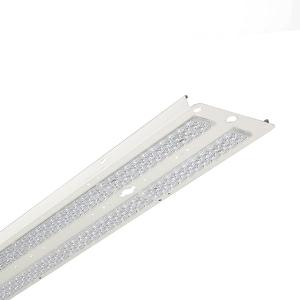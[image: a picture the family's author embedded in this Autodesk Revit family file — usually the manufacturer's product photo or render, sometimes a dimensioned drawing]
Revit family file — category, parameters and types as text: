
# Revit family: 3f_filippi_-_kit_led_retrofit_per_schermo_in_vetro_3f_filippi_-_a5212_-_kit_led_i3f_76_a3f_91_-_l1565_-__7bcecbea5744f0cb
name_source: partatom
category: Lighting Fixtures
units: mm (PartAtom-declared; Revit-internal decimal feet)

## family parameters
Cut with Voids When Loaded = No
Host = Face
Light Source = No
Part Type = Normal
Room Calculation Point = No
Round Connector Dimension = Use Diameter
Shared = No

## types (1)
- 3F Filippi - Kit LED Retrofit per schermo in vetro (1 x LED, 11260 lm, 74 W, 4000 K)
    Apparent Load = 74 VA
    Approval mark = ENEC
    CIE Flux Codes = 77 93 99 100 100
    Color Rendering = 80
    Color Temperature = 4000 K
    Control Gear = Electronic ballast
    Default Elevation = 1800 mm
    Description = Led retrofit kit suitable for Fluorescent Beta 2x i3F 76 and A3F 91 luminaires.

ILLUMINOTECHNICAL
Luminous efficiency 100% (DLOR 100%, ULOR 0%).
Initial luminous flux of the luminaire 11260 lm.
Symmetric concentrated distribution.
Installation Interdistance Transv.D = 0.57 x hu - Long.D = 1.12 x hu.
Tabular UGR (CIE 117 - 4H-8H; S=0.25H; 70/50/20): RUG 17.5 - 19.7.
Beam angle: 36° - 73°.
Luminous efficacy 152 lm/W.
Lifetime (L93/B10): 30000 h. (tq+25°C)
Lifetime (L90/B10): 50000 h. (tq+25°C)
Lifetime (L85/B10): 80000 h. (tq+25°C)
Lifetime (L80/B10): 100000 h. (tq+25°C)
Lifetime (L85/B10): 50000 h. (tq+40°C)
Sudden decreased luminous flux after 50000 hours: 0% (C0).
Photobiological safety in compliance with IEC/TR 62778: RG0 risk exempt, (IEC 62471).
In compliance with IEC/EN 62722-2-1 - IEC/EN 62717 standards.

SOURCE
2 linear LED modules 40W/840.
Energy efficiency class (UE 2019/2020 - UE 2019/2015): C.
CIE 13.3 Colour rendering index: CRI >80 (R9 <50%).
IES TM-30 Fidelity Index: Rf = 84 Rg = 95.
CCT nominal colour temperature 4000 K.
Colour initial tolerance (MacAdam): SDCM 3.

MECHANICAL
Gear-tray unit in hot-galvanised steel, painted in white polyester, fixed to the housing by means of "Ribloc" rapid devices in galvanised steel, hinged opening.
Transparent methacrylate (PMMA) concentrated distribution lenses with flat external surface.
Luminaire with limited surface temperature. - D - (EN 60598-2-24)
Dimensions: 1565x235 mm, height 105 mm. Weight 3.395 kg.
Glow-wire test resistance 850°C.

ELECTRICAL
Halogen Free electronic wiring 230V-50/60Hz, power factor 0.95, THD <25%, constant output current, class I, 1 driver.
Power of the luminaire 74 W.
CE - IEC 60598-1 - EN 60598-1.
SAFE FLICKER: PstLM=<1 and SVM=<0.4 (IEC TR 61547-1 and IEC TR 63158), to ensure a more comfortable and safe light.
Luminaire compliant with EN 60598-2-22 for power supply from a centralised emergency system CPSS (Central Power Supply System), not incorporated in the luminaire - high risk areas excluded. The default power and flux are 100% in AC and 100% in DC.
Ambient temperature from -20°C to +40°C.
Temperature class T6 max 85°C.
Relative humidity UR: <85%.

INSTALLATION
Retrofit.
Correct installation of the retrofit LED kit, compliant with EN 60598-1 and CE marked, inside the 3F Filippi - Beta 2x i3F 76 and A3F 91 Fluorescent luminaires must be only carried out by qualified personnel to ensure compliance with the national installation standards.
Attention: to maintain the degree of protection of the device and for the purposes of validity of the guarantee of the new retrofit kits, it is imperative to replace the old cable guides (on the body of the device) with the new ones supplied.
All accessories dedicated to this product are available on the Catalog and on our website www.3F-Filippi.com.

WARNING
Fixture not suitable for cold stores with an ambient temperature <0°C and/or relative humidity >85%.
Luminaire designed for disposal/recycling at end-of-life.
Replaceable (LED only) light source by a professional. Replaceable control gear by a professional.
    Height = 105 mm
    Lamp = 1 x LED
    Lamp Light Flux = 11260 lm
    Lamp Power = 74 W
    Lamp count = 1
    Length = 1565 mm
    Lifetime = 50000 h
    Luminous efficacy = 152 lm/W
    Manufacturer = 3F Filippi
    ModVariant = No
    Model = 3F Filippi - A5212 - Kit LED i3F 76,A3F 91 - L1565 - L 2x40W CONC
    Mounting Place = Ceiling
    Mounting Type = Surface mounted
    Number of Poles = 1
    OnlyDefault = Yes
    Power Factor = 1
    Product Name = 3F Filippi - Kit LED Retrofit per schermo in vetro
    Product group = ceiling mounted luminaire
    ProductGroupID = 3
    Protection Class = Protection class I
    Protection Degree = Degree of protection
    RLX_Detail_Level = 1
    RLX_Emergency_Light_Flux = 0 lm
    RLX_Emergency_Type = 0
    RLX_Emergency_Type_DB = No
    RlxData = <blob elided: 68885 chars, md5=a219a7c4>
    Socket = socket
    Standby Power = 0 W
    System Light Flux = 11260 lm
    System Power = 74 W
    Type Comments = Product without accessories
    Type Image = 3ffilippi_a5212.jpg
    URL = http://relux.com
    VarID = ---
    Voltage = 0 V
    Weight = 0.00 kg
    Width = 235 mm

## geometry (parser evidence)
native form markers: Blend x4, Sweep x9
no freeform markers — native parametric forms only
